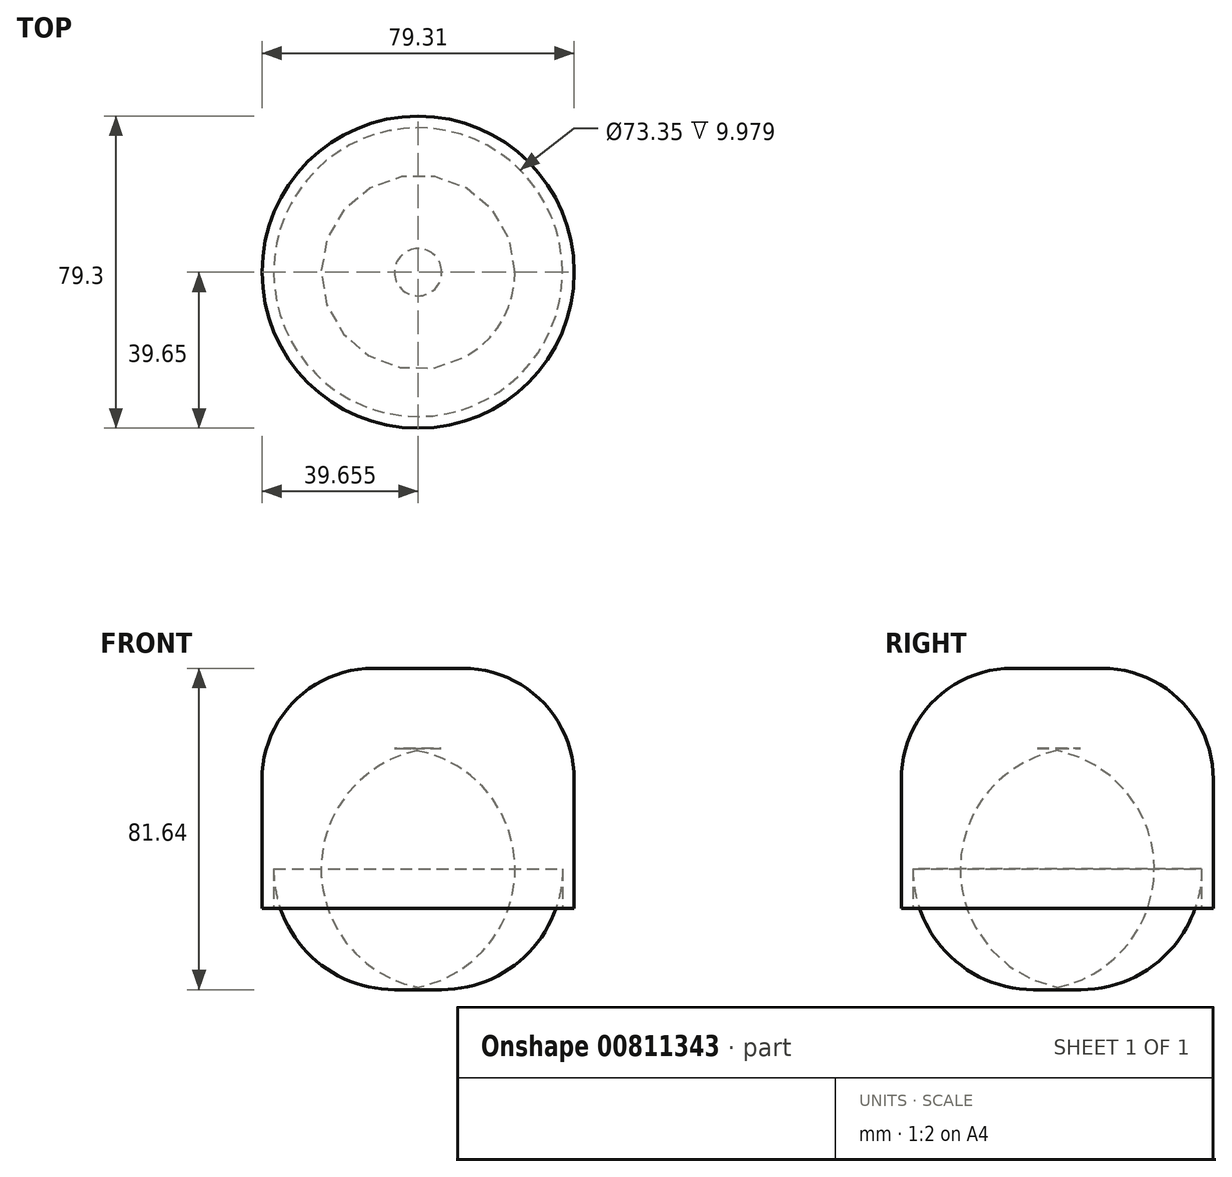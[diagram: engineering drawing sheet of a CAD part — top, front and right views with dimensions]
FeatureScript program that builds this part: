
annotation { "Feature Type Name" : "Feature", "Feature Type Description" : "" }
export const myFeature = defineFeature(function(context is Context, id is Id, definition is map)
    precondition{}
    {
        {
            var Q0;
            Q0=qCreatedBy(makeId("Top.planeOp"),FACE);
            var sketch = newSketch(context, id + "F0", { "sketchPlane" : qUnion([Q0])});
            skCircle(sketch, "E0", {"center": v(-4, 10.15) * mm, "radius": 39.65 * mm});
            skSolve(sketch);
        }
        {
            var Q0;
            Q0=makeQuery(id+"F0.imprint","IMPRINT",FACE,{"disambiguationData":[TD([[makeQuery(id+"F0.imprint","IMPRINT",EDGE,{"derivedFrom":sQuery(id+"F0.wireOp",EDGE,"E0")}),1.0]])]});
            extrude(context, id + "F1", {"entities" : qUnion([Q0]), "depth" : 60.96 * mm, "offsetDistance" : 25.4 * mm});
        }
        {
            var Q0;
            Q0=makeQuery(id+"F1.opExtrude","CAP_FACE",FACE,{"disambiguationData":[OSD([sQuery(id+"F0.wireOp",EDGE,"E0")])],"isStart":false});
            fillet(context, id + "F2", {"entities" : qUnion([Q0]), "radius" : 28.2 * mm, "tangentPropagation" : true, "allowEdgeOverflow" : false});
        }
        {
            var Q0;
            Q0=makeQuery(id+"F1.opExtrude","CAP_FACE",FACE,{"disambiguationData":[OSD([sQuery(id+"F0.wireOp",EDGE,"E0")])],"isStart":true});
            var sketch = newSketch(context, id + "F3", { "sketchPlane" : qUnion([Q0])});
            skCircle(sketch, "E1", {"center": v(-4, -10.15) * mm, "radius": 36.68 * mm});
            skSolve(sketch);
        }
        {
            var Q0;
            Q0 = qSketchRegion(id + "F3", true);
            extrude(context, id + "F4", {"entities" : qUnion([Q0]), "operationType" : NewBodyOperationType.REMOVE, "oppositeDirection" : true, "depth" : 40.64 * mm, "offsetDistance" : 25.4 * mm});
        }
        {
            var Q0;
            Q0=makeQuery(id+"F4.boolean.opBoolean","COPY",FACE,{"derivedFrom":makeQuery(id+"F4.opExtrude","CAP_FACE",FACE,{"disambiguationData":[OSD([sQuery(id+"F3.wireOp",EDGE,"E1")])],"isStart":false})});
            fillet(context, id + "F5", {"entities" : qUnion([Q0]), "radius" : 30.66 * mm, "tangentPropagation" : true, "allowEdgeOverflow" : false});
        }
    });
